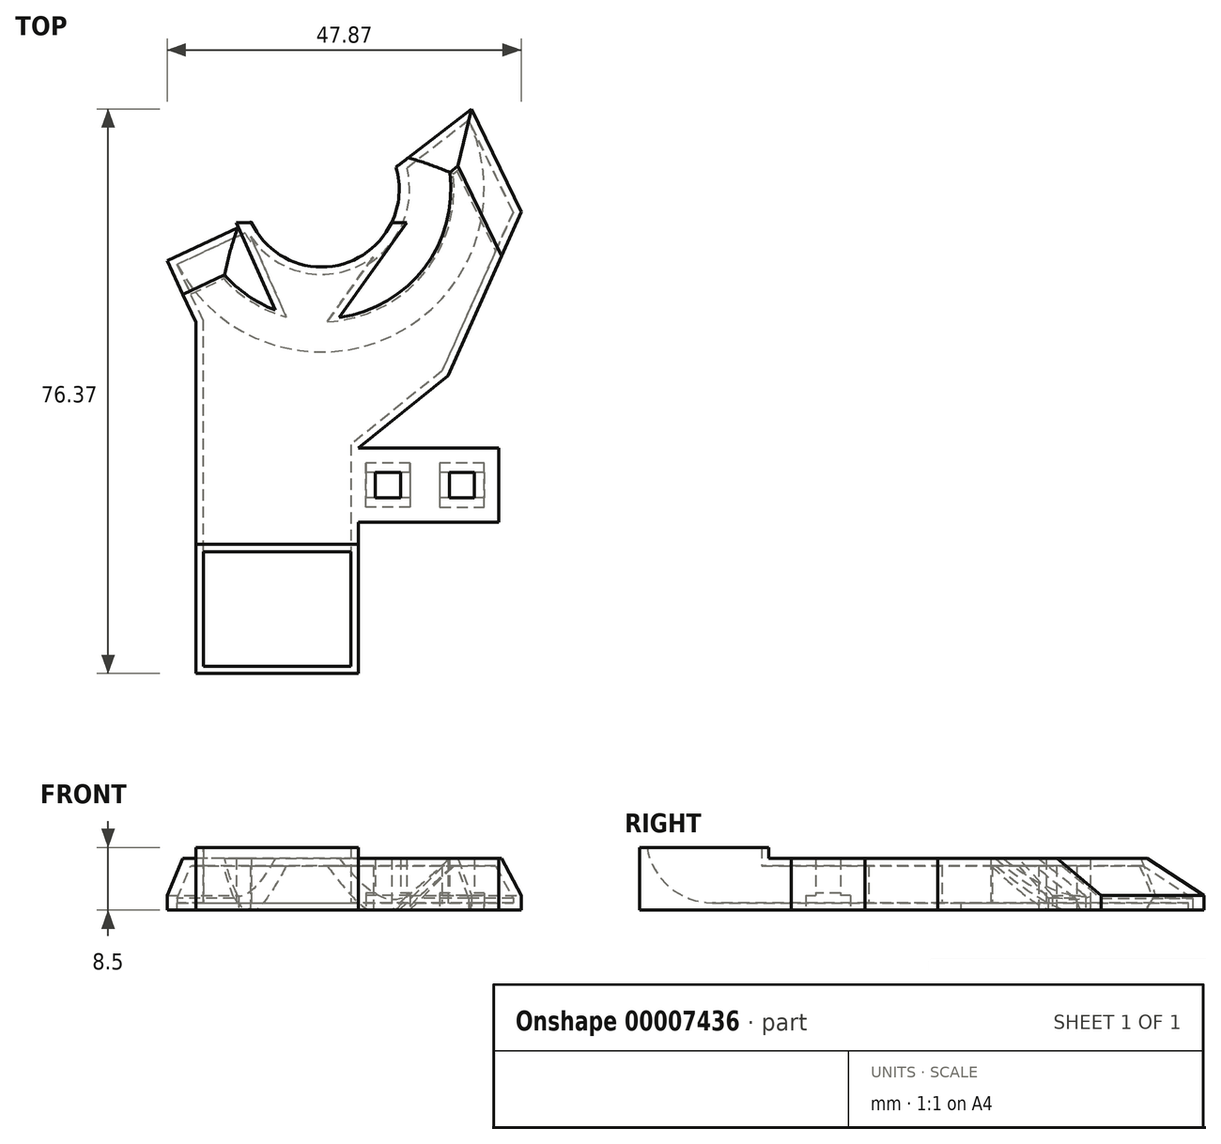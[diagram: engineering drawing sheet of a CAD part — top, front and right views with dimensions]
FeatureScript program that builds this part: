
annotation { "Feature Type Name" : "Feature", "Feature Type Description" : "" }
export const myFeature = defineFeature(function(context is Context, id is Id, definition is map)
    precondition{}
    {
        {
            var Q0;
            Q0=qCreatedBy(makeId("Top.planeOp"),FACE);
            var sketch = newSketch(context, id + "F0", { "sketchPlane" : qUnion([Q0])});
            skLineSegment(sketch, "E0", {"start": v(0, 0) * mm, "end": v(0, -12) * mm, "construction": true});
            skLineSegment(sketch, "E1", {"start": v(0, -12) * mm, "end": v(0, -21.5) * mm, "construction": true});
            skLineSegment(sketch, "E2", {"start": v(0, -12) * mm, "end": v(-5, -12) * mm, "construction": true});
            skLineSegment(sketch, "E3", {"start": v(-5, -12) * mm, "end": v(-15, -12) * mm, "construction": true});
            skLineSegment(sketch, "E4", {"start": v(0, -21.5) * mm, "end": v(-40, -21.5) * mm, "construction": true});
            skPoint(sketch, "E5", {"position": v(-24, 28) * mm});
            skLineSegment(sketch, "E6", {"start": v(-40, -21.5) * mm, "end": v(-40, -36.5) * mm, "construction": true});
            skLineSegment(sketch, "E7", {"start": v(-40, -36.5) * mm, "end": v(-20, -36.5) * mm, "construction": true});
            skLineSegment(sketch, "E8", {"start": v(-20, -36.5) * mm, "end": v(-20, -21.5) * mm, "construction": true});
            skLineSegment(sketch, "E9", {"start": v(-32, 43.5) * mm, "end": v(-32, 23.5) * mm, "construction": true});
            skLineSegment(sketch, "E10", {"start": v(-32, 23.5) * mm, "end": v(-16, 23.5) * mm, "construction": true});
            skLineSegment(sketch, "E11", {"start": v(-16, 23.5) * mm, "end": v(-16, 43.5) * mm, "construction": true});
            skLineSegment(sketch, "E12", {"start": v(-16, 43.5) * mm, "end": v(-32, 43.5) * mm, "construction": true});
            skLineSegment(sketch, "E13", {"start": v(-24, 28) * mm, "end": v(-24, 23.5) * mm, "construction": true});
            skSolve(sketch);
        }
        {
            var Q0;
            Q0=qCreatedBy(makeId("Top.planeOp"),FACE);
            var sketch = newSketch(context, id + "F1", { "sketchPlane" : qUnion([Q0])});
            skLineSegment(sketch, "E14", {"start": v(-19, -7) * mm, "end": v(-19, -17) * mm});
            skLineSegment(sketch, "E15", {"start": v(-19, -17) * mm, "end": v(-19, -37.5) * mm});
            skLineSegment(sketch, "E16", {"start": v(-19, -37.5) * mm, "end": v(-41, -37.5) * mm});
            skLineSegment(sketch, "E17", {"start": v(-41, -37.5) * mm, "end": v(-41, -15) * mm});
            skLineSegment(sketch, "E18", {"start": v(-41, -15) * mm, "end": v(-41, 10) * mm});
            skPoint(sketch, "E19.0", {"position": v(-15, -12) * mm});
            skPoint(sketch, "E20.0", {"position": v(-5, -12) * mm});
            skLineSegment(sketch, "E21.0", {"start": v(-40, -21.5) * mm, "end": v(-40, -36.5) * mm});
            skLineSegment(sketch, "E22.0", {"start": v(-20, -36.5) * mm, "end": v(-20, -21.5) * mm});
            skLineSegment(sketch, "E23.rect.bottom", {"start": v(-12, -10.3) * mm, "end": v(-18, -10.3) * mm});
            skLineSegment(sketch, "E23.rect.top", {"start": v(-12, -13.7) * mm, "end": v(-18, -13.7) * mm});
            skLineSegment(sketch, "E23.rect.left", {"start": v(-12, -10.3) * mm, "end": v(-12, -13.7) * mm});
            skLineSegment(sketch, "E23.rect.right", {"start": v(-18, -10.3) * mm, "end": v(-18, -13.7) * mm});
            skLineSegment(sketch, "E24.rect.bottom", {"start": v(-2, -10.3) * mm, "end": v(-8, -10.3) * mm});
            skLineSegment(sketch, "E24.rect.top", {"start": v(-2, -13.7) * mm, "end": v(-8, -13.7) * mm});
            skLineSegment(sketch, "E24.rect.left", {"start": v(-2, -10.3) * mm, "end": v(-2, -13.7) * mm});
            skLineSegment(sketch, "E24.rect.right", {"start": v(-8, -10.3) * mm, "end": v(-8, -13.7) * mm});
            skLineSegment(sketch, "E25", {"start": v(-8, -10.3) * mm, "end": v(-12, -10.3) * mm, "construction": true});
            skLineSegment(sketch, "E26", {"start": v(-2, -10.3) * mm, "end": v(-2, -9) * mm});
            skLineSegment(sketch, "E27", {"start": v(-2, -9) * mm, "end": v(-8, -9) * mm});
            skLineSegment(sketch, "E28", {"start": v(-8, -9) * mm, "end": v(-8, -10.3) * mm});
            skLineSegment(sketch, "E29", {"start": v(-8, -13.7) * mm, "end": v(-8, -15) * mm});
            skLineSegment(sketch, "E30", {"start": v(-8, -15) * mm, "end": v(-2, -15) * mm});
            skLineSegment(sketch, "E31", {"start": v(-2, -15) * mm, "end": v(-2, -13.7) * mm});
            skLineSegment(sketch, "E32", {"start": v(-12, -10.3) * mm, "end": v(-12, -9) * mm});
            skLineSegment(sketch, "E33", {"start": v(-12, -9) * mm, "end": v(-18, -9) * mm});
            skLineSegment(sketch, "E34", {"start": v(-18, -9) * mm, "end": v(-18, -10.3) * mm});
            skLineSegment(sketch, "E35", {"start": v(-12, -13.7) * mm, "end": v(-12, -15) * mm});
            skLineSegment(sketch, "E36", {"start": v(-12, -15) * mm, "end": v(-18, -15) * mm});
            skLineSegment(sketch, "E37", {"start": v(-18, -15) * mm, "end": v(-18, -13.7) * mm});
            skLineSegment(sketch, "E38.rect.bottom", {"start": v(-13.3, -10.3) * mm, "end": v(-16.7, -10.3) * mm});
            skLineSegment(sketch, "E38.rect.top", {"start": v(-13.3, -13.7) * mm, "end": v(-16.7, -13.7) * mm});
            skLineSegment(sketch, "E38.rect.left", {"start": v(-13.3, -10.3) * mm, "end": v(-13.3, -13.7) * mm});
            skLineSegment(sketch, "E38.rect.right", {"start": v(-16.7, -10.3) * mm, "end": v(-16.7, -13.7) * mm});
            skLineSegment(sketch, "E39.rect.bottom", {"start": v(-3.3, -10.3) * mm, "end": v(-6.7, -10.3) * mm});
            skLineSegment(sketch, "E39.rect.top", {"start": v(-3.3, -13.7) * mm, "end": v(-6.7, -13.7) * mm});
            skLineSegment(sketch, "E39.rect.left", {"start": v(-3.3, -10.3) * mm, "end": v(-3.3, -13.7) * mm});
            skLineSegment(sketch, "E39.rect.right", {"start": v(-6.7, -10.3) * mm, "end": v(-6.7, -13.7) * mm});
            skLineSegment(sketch, "E40", {"start": v(-19, -17) * mm, "end": v(0, -17) * mm});
            skLineSegment(sketch, "E41", {"start": v(0, -17) * mm, "end": v(0, -7) * mm});
            skLineSegment(sketch, "E42", {"start": v(0, -7) * mm, "end": v(-19, -7) * mm});
            skPoint(sketch, "E43.0", {"position": v(-24, 28) * mm});
            skCircle(sketch, "E44", {"center": v(-24, 28) * mm, "radius": 10.5 * mm});
            skCircle(sketch, "E45", {"center": v(-24, 28) * mm, "radius": 23 * mm});
            skLineSegment(sketch, "E46", {"start": v(-41, 10) * mm, "end": v(-44.86, 18.31) * mm});
            skLineSegment(sketch, "E47", {"start": v(-44.86, 18.31) * mm, "end": v(-33.54, 23.6) * mm});
            skLineSegment(sketch, "E48", {"start": v(-13.93, 30.98) * mm, "end": v(-3.73, 38.87) * mm});
            skLineSegment(sketch, "E49", {"start": v(-3.73, 38.87) * mm, "end": v(3.01, 24.93) * mm});
            skLineSegment(sketch, "E50", {"start": v(3.01, 24.93) * mm, "end": v(-6.89, 2.8) * mm});
            skLineSegment(sketch, "E51", {"start": v(-6.89, 2.8) * mm, "end": v(-19, -7) * mm});
            skSolve(sketch);
        }
        {
            var Q0;
            Q0=qCreatedBy(makeId("Top.planeOp"),FACE);
            var sketch = newSketch(context, id + "F2", { "sketchPlane" : qUnion([Q0])});
            skLineSegment(sketch, "E52.0", {"start": v(-32, 23.5) * mm, "end": v(-16, 23.5) * mm});
            skPoint(sketch, "E53.0", {"position": v(-20, -21.5) * mm});
            skPoint(sketch, "E54.0", {"position": v(-40, -21.5) * mm});
            skLineSegment(sketch, "E55", {"start": v(-40, -21.5) * mm, "end": v(-20, -21.5) * mm, "construction": true});
            skLineSegment(sketch, "E56", {"start": v(-30, -21.5) * mm, "end": v(-24, 23.5) * mm, "construction": true});
            skCircle(sketch, "E57.0", {"center": v(-24, 28) * mm, "radius": 10.5 * mm});
            skLineSegment(sketch, "E58", {"start": v(-12.5, 23.5) * mm, "end": v(-26.67, 3.5) * mm});
            skLineSegment(sketch, "E59", {"start": v(-16, 23.5) * mm, "end": v(-12.5, 23.5) * mm});
            skLineSegment(sketch, "E60", {"start": v(-32, 23.5) * mm, "end": v(-35.5, 23.5) * mm});
            skLineSegment(sketch, "E61", {"start": v(-35.5, 23.5) * mm, "end": v(-26.67, 3.5) * mm});
            skSolve(sketch);
        }
        {
            var Q0;
            Q0=makeQuery(id+"F1.imprint","IMPRINT",FACE,{"disambiguationData":[TD([[makeQuery(id+"F1.imprint","IMPRINT",EDGE,{"derivedFrom":sQuery(id+"F1.wireOp",EDGE,"E14")}),-1.0]])]});
            var Q1;
            {var subQ0=sQuery(id+"F1.wireOp",EDGE,"E47");Q1=makeQuery(id+"F1.imprint","IMPRINT",FACE,{"disambiguationData":[TD([[makeQuery(id+"F1.imprint","IMPRINT",EDGE,{"derivedFrom":subQ0}),-1.0]])]});}
            extrude(context, id + "F3", {"entities" : qUnion([Q0, Q1]), "depth" : 7 * mm});
        }
        {
            var Q0;
            Q0=makeQuery(id+"F3.opExtrude","CAP_FACE",FACE,{"disambiguationData":[OSD([sQuery(id+"F1.wireOp",EDGE,"726e78eb-56e2-47ea-b6f5-47efc0460c47"),sQuery(id+"F1.wireOp",EDGE,"fa15ef6f-fb31-48d0-98cb-08a9dc3e37e7"),sQuery(id+"F1.wireOp",EDGE,"288b6f4e-36c9-46e4-8515-fd5ad4e604e2"),sQuery(id+"F1.wireOp",EDGE,"37ce52b8-0f7f-4cb6-b0b0-6c3cf62d658f"),sQuery(id+"F1.wireOp",EDGE,"6ad6b573-81d0-4507-a461-966eaf882e56"),sQuery(id+"F1.wireOp",EDGE,"1b400430-0135-404f-adc2-64bbd31526d7"),sQuery(id+"F1.wireOp",EDGE,"E14"),sQuery(id+"F1.wireOp",EDGE,"E15"),sQuery(id+"F1.wireOp",EDGE,"E16"),sQuery(id+"F1.wireOp",EDGE,"E17"),sQuery(id+"F1.wireOp",EDGE,"E18"),sQuery(id+"F1.wireOp",EDGE,"71707b2f-24f5-41ae-93e4-82e1504ae774")])],"isStart":false});
            var sketch = newSketch(context, id + "F4", { "sketchPlane" : qUnion([Q0])});
            skLineSegment(sketch, "E62.0", {"start": v(-19, -7) * mm, "end": v(-19, -37.5) * mm});
            skLineSegment(sketch, "E63.0", {"start": v(-19, -37.5) * mm, "end": v(-41, -37.5) * mm});
            skLineSegment(sketch, "E64.0", {"start": v(-41, -37.5) * mm, "end": v(-41, -37.5) * mm});
            skLineSegment(sketch, "E65.0", {"start": v(0, -21.5) * mm, "end": v(-40, -21.5) * mm});
            skLineSegment(sketch, "E66", {"start": v(-19, -20) * mm, "end": v(-41, -20) * mm});
            skSolve(sketch);
        }
        {
            var Q0;
            {var subQ2=sQuery(id+"F4.wireOp",EDGE,"E63.0");Q0=makeQuery(id+"F4.imprint","IMPRINT",FACE,{"disambiguationData":[TD([[makeQuery(id+"F4.imprint","IMPRINT",EDGE,{"derivedFrom":subQ2}),-1.0]])]});}
            extrude(context, id + "F5", {"entities" : qUnion([Q0]), "operationType" : NewBodyOperationType.ADD, "depth" : 1.5 * mm});
        }
        {
            var Q0;
            {var subQ5=sQuery(id+"F2.wireOp",EDGE,"E58");Q0=makeQuery(id+"F2.imprint","IMPRINT",FACE,{"disambiguationData":[TD([[makeQuery(id+"F2.imprint","IMPRINT",EDGE,{"derivedFrom":subQ5}),-1.0]])]});}
            var Q1;
            Q1=makeQuery(id+"F3.opExtrude","CAP_FACE",FACE,{"disambiguationData":[OSD([sQuery(id+"F1.wireOp",EDGE,"E14"),sQuery(id+"F1.wireOp",EDGE,"E15"),sQuery(id+"F1.wireOp",EDGE,"E16"),sQuery(id+"F1.wireOp",EDGE,"E17"),sQuery(id+"F1.wireOp",EDGE,"E18"),sQuery(id+"F1.wireOp",EDGE,"E44"),sQuery(id+"F1.wireOp",EDGE,"E46"),sQuery(id+"F1.wireOp",EDGE,"E47"),sQuery(id+"F1.wireOp",EDGE,"E48"),sQuery(id+"F1.wireOp",EDGE,"E49"),sQuery(id+"F1.wireOp",EDGE,"E50"),sQuery(id+"F1.wireOp",EDGE,"E51")])],"isStart":false});
            extrude(context, id + "F6", {"entities" : qUnion([Q0]), "endBound" : BoundingType.UP_TO_SURFACE, "endBoundEntityFace" : qUnion([Q1]), "depth" : 25 * mm});
        }
        {
            var Q0;
            Q0=makeQuery(id+"F3.opExtrude","CAP_EDGE",EDGE,{"disambiguationData":[OSD([sQuery(id+"F1.wireOp",EDGE,"E44")])],"isStart":false});
            var Q1;
            {var subQ0=sQuery(id+"F2.wireOp",EDGE,"E57.0");Q1=makeQuery(id+"F6.opExtrude","TWEAK_EDGE",EDGE,{"derivedFrom":[makeQuery(id+"F2.imprint","IMPRINT",EDGE,{"disambiguationData":[TD([[makeQuery(id+"F2.imprint","INTERSECT",VERTEX,{"derivedFrom":[sQuery(id+"F2.wireOp",EDGE,"KVkim7sW-yz6l-oKEe-9N2c-gesbX2qdFGWd"),subQ0]}),-1.0]])],"derivedFrom":subQ0}),makeQuery(id+"F3.opExtrude","CAP_FACE",FACE,{"disambiguationData":[OSD([sQuery(id+"F1.wireOp",EDGE,"E14"),sQuery(id+"F1.wireOp",EDGE,"E15"),sQuery(id+"F1.wireOp",EDGE,"E16"),sQuery(id+"F1.wireOp",EDGE,"E17"),sQuery(id+"F1.wireOp",EDGE,"E18"),sQuery(id+"F1.wireOp",EDGE,"E44"),sQuery(id+"F1.wireOp",EDGE,"E46"),sQuery(id+"F1.wireOp",EDGE,"E47"),sQuery(id+"F1.wireOp",EDGE,"E48"),sQuery(id+"F1.wireOp",EDGE,"E49"),sQuery(id+"F1.wireOp",EDGE,"E50"),sQuery(id+"F1.wireOp",EDGE,"E51")])],"isStart":false})]});}
            chamfer(context, id + "F7", {"entities" : qUnion([Q0, Q1]), "width" : 7 * mm, "tangentPropagation" : true});
        }
        {
            var Q0;
            Q0=makeQuery(id+"F3.opExtrude","CAP_EDGE",EDGE,{"disambiguationData":[OSD([sQuery(id+"F1.wireOp",EDGE,"E47")])],"isStart":false});
            var Q1;
            Q1=makeQuery(id+"F3.opExtrude","CAP_EDGE",EDGE,{"disambiguationData":[OSD([sQuery(id+"F1.wireOp",EDGE,"E49")])],"isStart":false});
            var Q2;
            Q2=makeQuery(id+"F3.opExtrude","CAP_EDGE",EDGE,{"disambiguationData":[OSD([sQuery(id+"F1.wireOp",EDGE,"E48")])],"isStart":false});
            chamfer(context, id + "F8", {"entities" : qUnion([Q0, Q1, Q2]), "width" : 5 * mm, "tangentPropagation" : true});
        }
        {
            var Q0;
            Q0=qCreatedBy(makeId("Top.planeOp"),FACE);
            var sketch = newSketch(context, id + "F9", { "sketchPlane" : qUnion([Q0])});
            skCircle(sketch, "E67.0", {"center": v(-24, 28) * mm, "radius": 23 * mm});
            skCircle(sketch, "E68.0", {"center": v(-24, 28) * mm, "radius": 10.5 * mm});
            skLineSegment(sketch, "E69.0", {"start": v(-44.86, 18.31) * mm, "end": v(-33.54, 23.6) * mm});
            skLineSegment(sketch, "E70.0", {"start": v(-13.93, 30.98) * mm, "end": v(-3.73, 38.87) * mm});
            skSolve(sketch);
        }
        {
            var Q0;
            Q0 = qSketchRegion(id + "F9", true);
            extrude(context, id + "F10", {"entities" : qUnion([Q0]), "operationType" : NewBodyOperationType.ADD, "oppositeDirection" : true, "depth" : 5 * mm});
        }
        {
            var Q0;
            Q0=makeQuery(id+"F10.opExtrude","CAP_FACE",FACE,{"disambiguationData":[OSD([sQuery(id+"F9.wireOp",EDGE,"1a944d00-084b-4ff9-9d19-91ccdd1f2c37.0"),sQuery(id+"F9.wireOp",EDGE,"9bbf65b2-a4d8-46b0-b6b6-1e68403ac3ce.0"),sQuery(id+"F9.wireOp",EDGE,"9d110ad1-58db-4db0-9e68-2a1495851d6b.0"),sQuery(id+"F9.wireOp",EDGE,"a38a0b3c-3594-412f-ae05-99f41588887f.0"),sQuery(id+"F9.wireOp",EDGE,"e33504a2-dc81-4a30-935b-ee4b6f65ec9a.0"),sQuery(id+"F9.wireOp",EDGE,"dfe0c6c7-b4f3-4899-ac4e-a66b8dc6344a.0"),sQuery(id+"F9.wireOp",EDGE,"97433154-32f2-4662-a443-5944fef1a110.0"),sQuery(id+"F9.wireOp",EDGE,"175b2ed6-e2aa-4d11-89b4-9663bcb69172")])],"isStart":false});
            var Q1;
            Q1=makeQuery(id+"F5.opExtrude","CAP_FACE",FACE,{"disambiguationData":[OSD([sQuery(id+"F4.wireOp",EDGE,"E62.0"),sQuery(id+"F4.wireOp",EDGE,"E63.0"),sQuery(id+"F4.wireOp",EDGE,"E64.0"),sQuery(id+"F4.wireOp",EDGE,"E66")])],"isStart":false});
            var Q2;
            Q2=makeQuery(id+"F3.opExtrude","SWEPT_BODY",BODY,{"disambiguationData":[OSD([sQuery(id+"F1.wireOp",EDGE,"726e78eb-56e2-47ea-b6f5-47efc0460c47"),sQuery(id+"F1.wireOp",EDGE,"fa15ef6f-fb31-48d0-98cb-08a9dc3e37e7"),sQuery(id+"F1.wireOp",EDGE,"288b6f4e-36c9-46e4-8515-fd5ad4e604e2"),sQuery(id+"F1.wireOp",EDGE,"37ce52b8-0f7f-4cb6-b0b0-6c3cf62d658f"),sQuery(id+"F1.wireOp",EDGE,"6ad6b573-81d0-4507-a461-966eaf882e56"),sQuery(id+"F1.wireOp",EDGE,"1b400430-0135-404f-adc2-64bbd31526d7"),sQuery(id+"F1.wireOp",EDGE,"E14"),sQuery(id+"F1.wireOp",EDGE,"E15"),sQuery(id+"F1.wireOp",EDGE,"E16"),sQuery(id+"F1.wireOp",EDGE,"E17"),sQuery(id+"F1.wireOp",EDGE,"E18"),sQuery(id+"F1.wireOp",EDGE,"71707b2f-24f5-41ae-93e4-82e1504ae774")])]});
            shell(context, id + "F11", {"entities" : qUnion([Q0, Q1]), "parts" : qUnion([Q2]), "thickness" : 1 * mm});
        }
        {
            var Q0;
            Q0=qCreatedBy(makeId("Right.planeOp"),FACE);
            var sketch = newSketch(context, id + "F12", { "sketchPlane" : qUnion([Q0])});
            skLineSegment(sketch, "E71", {"start": v(-51.08, 0) * mm, "end": v(58.7, 0) * mm});
            skLineSegment(sketch, "E72", {"start": v(58.7, 0) * mm, "end": v(58.7, -26.43) * mm});
            skLineSegment(sketch, "E73", {"start": v(58.7, -26.43) * mm, "end": v(-51.08, -26.43) * mm});
            skLineSegment(sketch, "E74", {"start": v(-51.08, -26.43) * mm, "end": v(-51.08, 0) * mm});
            skSolve(sketch);
        }
        {
            var Q0;
            Q0 = qSketchRegion(id + "F12", true);
            extrude(context, id + "F13", {"entities" : qUnion([Q0]), "operationType" : NewBodyOperationType.REMOVE, "oppositeDirection" : true, "depth" : 100 * mm, "hasSecondDirection" : true, "secondDirectionOppositeDirection" : false, "secondDirectionDepth" : 100 * mm});
        }
        {
            var Q0;
            Q0=makeQuery(id+"F11.opShell","OFFSET_EDGE",EDGE,{"disambiguationData":[OSD([sQuery(id+"F1.wireOp",EDGE,"E16")])]});
            fillet(context, id + "F14", {"entities" : qUnion([Q0]), "radius" : 9 * mm, "tangentPropagation" : true, "allowEdgeOverflow" : false});
        }
        {
            var Q0;
            {var subQ1=sQuery(id+"F1.wireOp",EDGE,"E23.rect.left");Q0=makeQuery(id+"F1.imprint","IMPRINT",FACE,{"disambiguationData":[TD([[makeQuery(id+"F1.imprint","IMPRINT",EDGE,{"derivedFrom":subQ1}),-1.0]])]});}
            var Q1;
            {var subQ3=sQuery(id+"F1.wireOp",EDGE,"E35");Q1=makeQuery(id+"F1.imprint","IMPRINT",FACE,{"disambiguationData":[TD([[makeQuery(id+"F1.imprint","IMPRINT",EDGE,{"derivedFrom":subQ3}),-1.0]])]});}
            var Q2;
            {var subQ3=sQuery(id+"F1.wireOp",EDGE,"E32");Q2=makeQuery(id+"F1.imprint","IMPRINT",FACE,{"disambiguationData":[TD([[makeQuery(id+"F1.imprint","IMPRINT",EDGE,{"derivedFrom":subQ3}),1.0]])]});}
            var Q3;
            {var subQ1=sQuery(id+"F1.wireOp",EDGE,"E23.rect.right");Q3=makeQuery(id+"F1.imprint","IMPRINT",FACE,{"disambiguationData":[TD([[makeQuery(id+"F1.imprint","IMPRINT",EDGE,{"derivedFrom":subQ1}),1.0]])]});}
            var Q4;
            Q4=makeQuery(id+"F1.imprint","IMPRINT",FACE,{"disambiguationData":[TD([[makeQuery(id+"F1.imprint","IMPRINT",EDGE,{"derivedFrom":sQuery(id+"F1.wireOp",EDGE,"E14")}),1.0]])]});
            var Q5;
            {var subQ1=sQuery(id+"F1.wireOp",EDGE,"E24.rect.right");Q5=makeQuery(id+"F1.imprint","IMPRINT",FACE,{"disambiguationData":[TD([[makeQuery(id+"F1.imprint","IMPRINT",EDGE,{"derivedFrom":subQ1}),1.0]])]});}
            var Q6;
            {var subQ2=sQuery(id+"F1.wireOp",EDGE,"E26");Q6=makeQuery(id+"F1.imprint","IMPRINT",FACE,{"disambiguationData":[TD([[makeQuery(id+"F1.imprint","IMPRINT",EDGE,{"derivedFrom":subQ2}),1.0]])]});}
            var Q7;
            {var subQ0=sQuery(id+"F1.wireOp",EDGE,"E24.rect.left");Q7=makeQuery(id+"F1.imprint","IMPRINT",FACE,{"disambiguationData":[TD([[makeQuery(id+"F1.imprint","IMPRINT",EDGE,{"derivedFrom":subQ0}),-1.0]])]});}
            var Q8;
            {var subQ3=sQuery(id+"F1.wireOp",EDGE,"E29");Q8=makeQuery(id+"F1.imprint","IMPRINT",FACE,{"disambiguationData":[TD([[makeQuery(id+"F1.imprint","IMPRINT",EDGE,{"derivedFrom":subQ3}),1.0]])]});}
            extrude(context, id + "F15", {"entities" : qUnion([Q0, Q1, Q2, Q3, Q4, Q5, Q6, Q7, Q8]), "operationType" : NewBodyOperationType.ADD, "depth" : 7 * mm});
        }
        {
            var Q0;
            {var subQ3=sQuery(id+"F1.wireOp",EDGE,"E32");Q0=makeQuery(id+"F1.imprint","IMPRINT",FACE,{"disambiguationData":[TD([[makeQuery(id+"F1.imprint","IMPRINT",EDGE,{"derivedFrom":subQ3}),1.0]])]});}
            var Q1;
            {var subQ3=sQuery(id+"F1.wireOp",EDGE,"E35");Q1=makeQuery(id+"F1.imprint","IMPRINT",FACE,{"disambiguationData":[TD([[makeQuery(id+"F1.imprint","IMPRINT",EDGE,{"derivedFrom":subQ3}),-1.0]])]});}
            var Q2;
            {var subQ3=sQuery(id+"F1.wireOp",EDGE,"E29");Q2=makeQuery(id+"F1.imprint","IMPRINT",FACE,{"disambiguationData":[TD([[makeQuery(id+"F1.imprint","IMPRINT",EDGE,{"derivedFrom":subQ3}),1.0]])]});}
            var Q3;
            {var subQ2=sQuery(id+"F1.wireOp",EDGE,"E26");Q3=makeQuery(id+"F1.imprint","IMPRINT",FACE,{"disambiguationData":[TD([[makeQuery(id+"F1.imprint","IMPRINT",EDGE,{"derivedFrom":subQ2}),1.0]])]});}
            extrude(context, id + "F16", {"entities" : qUnion([Q0, Q1, Q2, Q3]), "operationType" : NewBodyOperationType.REMOVE, "depth" : (7 - 5) * mm});
        }
        {
            var Q0;
            {var subQ0=sQuery(id+"F1.wireOp",EDGE,"E24.rect.left");Q0=makeQuery(id+"F1.imprint","IMPRINT",FACE,{"disambiguationData":[TD([[makeQuery(id+"F1.imprint","IMPRINT",EDGE,{"derivedFrom":subQ0}),-1.0]])]});}
            var Q1;
            {var subQ1=sQuery(id+"F1.wireOp",EDGE,"E24.rect.right");Q1=makeQuery(id+"F1.imprint","IMPRINT",FACE,{"disambiguationData":[TD([[makeQuery(id+"F1.imprint","IMPRINT",EDGE,{"derivedFrom":subQ1}),1.0]])]});}
            var Q2;
            {var subQ1=sQuery(id+"F1.wireOp",EDGE,"E23.rect.left");Q2=makeQuery(id+"F1.imprint","IMPRINT",FACE,{"disambiguationData":[TD([[makeQuery(id+"F1.imprint","IMPRINT",EDGE,{"derivedFrom":subQ1}),-1.0]])]});}
            var Q3;
            {var subQ1=sQuery(id+"F1.wireOp",EDGE,"E23.rect.right");Q3=makeQuery(id+"F1.imprint","IMPRINT",FACE,{"disambiguationData":[TD([[makeQuery(id+"F1.imprint","IMPRINT",EDGE,{"derivedFrom":subQ1}),1.0]])]});}
            extrude(context, id + "F17", {"entities" : qUnion([Q0, Q1, Q2, Q3]), "operationType" : NewBodyOperationType.REMOVE, "depth" : (7 - 4.7) * mm});
        }
    });
